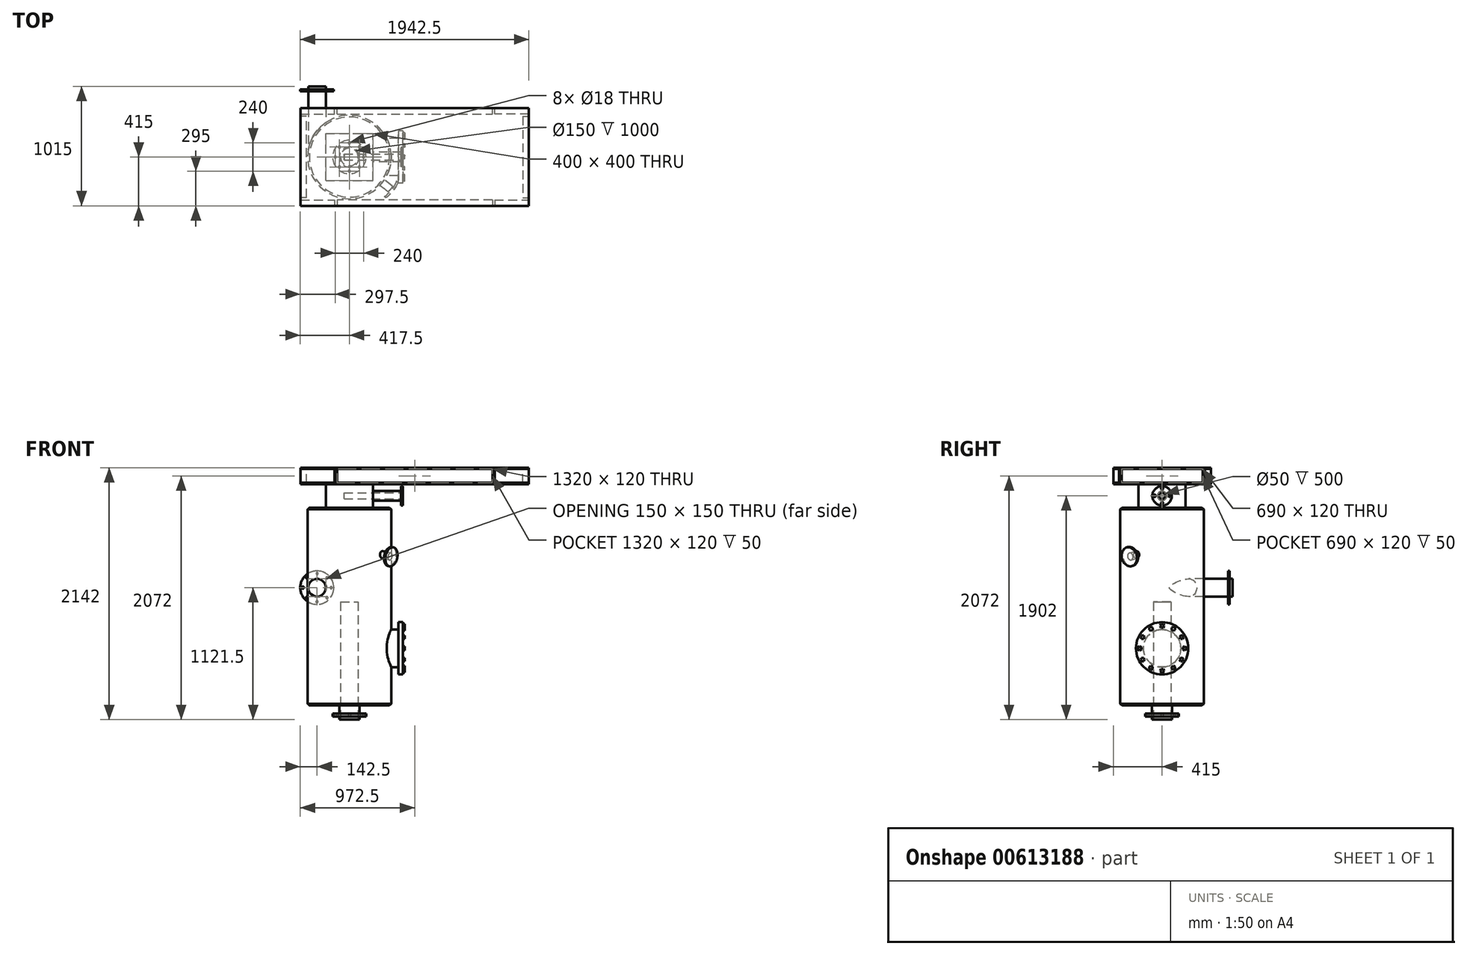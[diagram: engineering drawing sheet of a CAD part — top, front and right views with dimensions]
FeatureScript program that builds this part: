
annotation { "Feature Type Name" : "Feature", "Feature Type Description" : "" }
export const myFeature = defineFeature(function(context is Context, id is Id, definition is map)
    precondition{}
    {
        {
            var Q0;
            Q0=qCreatedBy(makeId("Front.planeOp"),FACE);
            var sketch = newSketch(context, id + "F0", { "sketchPlane" : qUnion([Q0])});
            skLineSegment(sketch, "E0.bottom", {"start": v(0, 0) * mm, "end": v(355, 0) * mm});
            skLineSegment(sketch, "E0.top", {"start": v(0, 1682) * mm, "end": v(355, 1682) * mm});
            skLineSegment(sketch, "E0.left", {"start": v(0, 0) * mm, "end": v(0, 1682) * mm});
            skLineSegment(sketch, "E0.right", {"start": v(355, 0) * mm, "end": v(355, 1682) * mm});
            skSolve(sketch);
        }
        {
            var Q0;
            Q0=makeQuery(id+"F0.imprint","IMPRINT",FACE,{"disambiguationData":[TD([[makeQuery(id+"F0.imprint","IMPRINT",EDGE,{"derivedFrom":sQuery(id+"F0.wireOp",EDGE,"E0.bottom")}),1.0]])]});
            var Q1;
            Q1=sQuery(id+"F0.wireOp",EDGE,"E0.left");
            revolve(context, id + "F1", {"entities" : qUnion([Q0]), "axis" : qUnion([Q1]), "revolveType" : RevolveType.FULL});
        }
        {
            var Q0;
            Q0=makeQuery(id+"F1.opRevolve","SWEPT_EDGE",EDGE,{"disambiguationData":[OSD([sQuery(id+"F0.wireOp",EDGE,"E0.top"),sQuery(id+"F0.wireOp",EDGE,"E0.right")])]});
            chamfer(context, id + "F2", {"entities" : qUnion([Q0]), "width" : 15 * mm, "tangentPropagation" : true});
        }
        {
            var Q0;
            Q0=qCreatedBy(makeId("Front.planeOp"),FACE);
            var sketch = newSketch(context, id + "F3", { "sketchPlane" : qUnion([Q0])});
            skCircle(sketch, "E1", {"center": v(-275, 1001.5) * mm, "radius": 75 * mm});
            skLineSegment(sketch, "E2", {"start": v(-355, 0) * mm, "end": v(-355, 1747) * mm});
            skSolve(sketch);
        }
        {
            var Q0;
            Q0 = qSketchRegion(id + "F3", true);
            extrude(context, id + "F4", {"entities" : qUnion([Q0]), "operationType" : NewBodyOperationType.ADD, "oppositeDirection" : true, "depth" : 600 * mm, "offsetDistance" : 25 * mm});
        }
        {
            var Q0;
            Q0=makeQuery(id+"F4.opExtrude","CAP_FACE",FACE,{"disambiguationData":[OSD([sQuery(id+"F3.wireOp",EDGE,"E1")])],"isStart":false});
            cPlane(context, id + "F5", {"entities" : qUnion([Q0]), "cplaneType" : CPlaneType.OFFSET, "offset" : 40 * mm, "oppositeDirection" : true, "width" : 150 * mm, "height" : 150 * mm});
        }
        {
            var Q0;
            Q0=qCreatedBy(id+"F5.planeOp",FACE);
            var sketch = newSketch(context, id + "F6", { "sketchPlane" : qUnion([Q0])});
            skCircle(sketch, "E3", {"center": v(275, 1001.5) * mm, "radius": 142.5 * mm});
            skSolve(sketch);
        }
        {
            var Q0;
            Q0=makeQuery(id+"F6.imprint","IMPRINT",FACE,{"disambiguationData":[TD([[makeQuery(id+"F6.imprint","IMPRINT",EDGE,{"derivedFrom":sQuery(id+"F6.wireOp",EDGE,"E3")}),1.0]])]});
            extrude(context, id + "F7", {"entities" : qUnion([Q0]), "operationType" : NewBodyOperationType.ADD, "depth" : 15 * mm, "offsetDistance" : 25 * mm});
        }
        {
            var Q0;
            Q0=makeQuery(id+"F7.opExtrude","CAP_FACE",FACE,{"disambiguationData":[OSD([sQuery(id+"F6.wireOp",EDGE,"E3")])],"isStart":false});
            var sketch = newSketch(context, id + "F8", { "sketchPlane" : qUnion([Q0])});
            skCircle(sketch, "E4", {"center": v(275.5, 881.5) * mm, "radius": 9 * mm});
            skCircle(sketch, "E5.1.0", {"center": v(360.21, 917) * mm, "radius": 9 * mm});
            skCircle(sketch, "E5.2.0", {"center": v(395, 1002) * mm, "radius": 9 * mm});
            skCircle(sketch, "E5.3.0", {"center": v(359.5, 1086.71) * mm, "radius": 9 * mm});
            skCircle(sketch, "E5.4.0", {"center": v(274.5, 1121.5) * mm, "radius": 9 * mm});
            skCircle(sketch, "E5.5.0", {"center": v(189.79, 1086) * mm, "radius": 9 * mm});
            skCircle(sketch, "E5.6.0", {"center": v(155, 1001) * mm, "radius": 9 * mm});
            skCircle(sketch, "E5.7.0", {"center": v(190.5, 916.29) * mm, "radius": 9 * mm});
            skPoint(sketch, "E5.center", {"position": v(275, 1001.5) * mm});
            skSolve(sketch);
        }
        {
            var Q0;
            Q0 = qSketchRegion(id + "F8", true);
            extrude(context, id + "F9", {"entities" : qUnion([Q0]), "operationType" : NewBodyOperationType.REMOVE, "oppositeDirection" : true, "depth" : 25 * mm, "offsetDistance" : 25 * mm});
        }
        {
            var Q0;
            Q0=qCreatedBy(makeId("Right.planeOp"),FACE);
            var sketch = newSketch(context, id + "F10", { "sketchPlane" : qUnion([Q0])});
            skCircle(sketch, "E6", {"center": v(0, 486) * mm, "radius": 160 * mm});
            skSolve(sketch);
        }
        {
            var Q0;
            Q0 = qSketchRegion(id + "F10", true);
            extrude(context, id + "F11", {"entities" : qUnion([Q0]), "operationType" : NewBodyOperationType.ADD, "depth" : 415 * mm, "offsetDistance" : 25 * mm});
        }
        {
            var Q0;
            Q0=makeQuery(id+"F11.opExtrude","CAP_FACE",FACE,{"disambiguationData":[OSD([sQuery(id+"F10.wireOp",EDGE,"E6")])],"isStart":false});
            var sketch = newSketch(context, id + "F12", { "sketchPlane" : qUnion([Q0])});
            skCircle(sketch, "E7", {"center": v(0, 486) * mm, "radius": 222.5 * mm});
            skSolve(sketch);
        }
        {
            var Q0;
            Q0=makeQuery(id+"F12.imprint","IMPRINT",FACE,{"disambiguationData":[TD([[makeQuery(id+"F12.imprint","IMPRINT",EDGE,{"derivedFrom":sQuery(id+"F12.wireOp",EDGE,"E7")}),1.0]])]});
            var Q1;
            Q1=makeQuery(id+"F12.imprint","IMPRINT",FACE,{"disambiguationData":[TD([[makeQuery(id+"F12.imprint","IMPRINT",EDGE,{"derivedFrom":makeQuery(id+"F11.opExtrude","CAP_EDGE",EDGE,{"disambiguationData":[OSD([sQuery(id+"F10.wireOp",EDGE,"E6")])],"isStart":false})}),1.0]])]});
            extrude(context, id + "F13", {"entities" : qUnion([Q0, Q1]), "operationType" : NewBodyOperationType.ADD, "depth" : 40 * mm, "offsetDistance" : 25 * mm});
        }
        {
            var Q0;
            Q0=makeQuery(id+"F13.opExtrude","CAP_FACE",FACE,{"disambiguationData":[OSD([sQuery(id+"F12.wireOp",EDGE,"E7")])],"isStart":false});
            var sketch = newSketch(context, id + "F14", { "sketchPlane" : qUnion([Q0])});
            skCircle(sketch, "E8.cCircle", {"center": v(0, 294.73) * mm, "radius": 14.58 * mm, "construction": true});
            skLineSegment(sketch, "E8.0", {"start": v(-8.42, 309.31) * mm, "end": v(8.42, 309.31) * mm});
            skLineSegment(sketch, "E8.1", {"start": v(8.42, 309.31) * mm, "end": v(16.84, 294.73) * mm});
            skLineSegment(sketch, "E8.2", {"start": v(16.84, 294.73) * mm, "end": v(8.42, 280.15) * mm});
            skLineSegment(sketch, "E8.3", {"start": v(8.42, 280.15) * mm, "end": v(-8.42, 280.15) * mm});
            skLineSegment(sketch, "E8.4", {"start": v(-8.42, 280.15) * mm, "end": v(-16.84, 294.73) * mm});
            skLineSegment(sketch, "E8.5", {"start": v(-16.84, 294.73) * mm, "end": v(-8.42, 309.31) * mm});
            skPoint(sketch, "E8.0.midPoint", {"position": v(0, 309.31) * mm});
            skCircle(sketch, "E9.1.0", {"center": v(95.63, 320.36) * mm, "radius": 14.58 * mm, "construction": true});
            skLineSegment(sketch, "E9.1.1", {"start": v(81.05, 311.94) * mm, "end": v(81.05, 328.78) * mm});
            skLineSegment(sketch, "E9.1.2", {"start": v(81.05, 328.78) * mm, "end": v(95.63, 337.2) * mm});
            skLineSegment(sketch, "E9.1.3", {"start": v(95.63, 337.2) * mm, "end": v(110.22, 328.78) * mm});
            skLineSegment(sketch, "E9.1.4", {"start": v(110.22, 328.78) * mm, "end": v(110.22, 311.94) * mm});
            skLineSegment(sketch, "E9.1.5", {"start": v(110.22, 311.94) * mm, "end": v(95.63, 303.52) * mm});
            skLineSegment(sketch, "E9.1.6", {"start": v(95.63, 303.52) * mm, "end": v(81.05, 311.94) * mm});
            skCircle(sketch, "E9.2.0", {"center": v(165.64, 390.37) * mm, "radius": 14.58 * mm, "construction": true});
            skLineSegment(sketch, "E9.2.1", {"start": v(157.22, 375.78) * mm, "end": v(148.8, 390.37) * mm});
            skLineSegment(sketch, "E9.2.2", {"start": v(148.8, 390.37) * mm, "end": v(157.22, 404.95) * mm});
            skLineSegment(sketch, "E9.2.3", {"start": v(157.22, 404.95) * mm, "end": v(174.06, 404.95) * mm});
            skLineSegment(sketch, "E9.2.4", {"start": v(174.06, 404.95) * mm, "end": v(182.48, 390.37) * mm});
            skLineSegment(sketch, "E9.2.5", {"start": v(182.48, 390.37) * mm, "end": v(174.06, 375.78) * mm});
            skLineSegment(sketch, "E9.2.6", {"start": v(174.06, 375.78) * mm, "end": v(157.22, 375.78) * mm});
            skCircle(sketch, "E9.3.0", {"center": v(191.27, 486) * mm, "radius": 14.58 * mm, "construction": true});
            skLineSegment(sketch, "E9.3.1", {"start": v(191.27, 469.16) * mm, "end": v(176.69, 477.58) * mm});
            skLineSegment(sketch, "E9.3.2", {"start": v(176.69, 477.58) * mm, "end": v(176.69, 494.42) * mm});
            skLineSegment(sketch, "E9.3.3", {"start": v(176.69, 494.42) * mm, "end": v(191.27, 502.84) * mm});
            skLineSegment(sketch, "E9.3.4", {"start": v(191.27, 502.84) * mm, "end": v(205.85, 494.42) * mm});
            skLineSegment(sketch, "E9.3.5", {"start": v(205.85, 494.42) * mm, "end": v(205.85, 477.58) * mm});
            skLineSegment(sketch, "E9.3.6", {"start": v(205.85, 477.58) * mm, "end": v(191.27, 469.16) * mm});
            skCircle(sketch, "E9.4.0", {"center": v(165.64, 581.63) * mm, "radius": 14.58 * mm, "construction": true});
            skLineSegment(sketch, "E9.4.1", {"start": v(174.06, 567.05) * mm, "end": v(157.22, 567.05) * mm});
            skLineSegment(sketch, "E9.4.2", {"start": v(157.22, 567.05) * mm, "end": v(148.8, 581.63) * mm});
            skLineSegment(sketch, "E9.4.3", {"start": v(148.8, 581.63) * mm, "end": v(157.22, 596.22) * mm});
            skLineSegment(sketch, "E9.4.4", {"start": v(157.22, 596.22) * mm, "end": v(174.06, 596.22) * mm});
            skLineSegment(sketch, "E9.4.5", {"start": v(174.06, 596.22) * mm, "end": v(182.48, 581.63) * mm});
            skLineSegment(sketch, "E9.4.6", {"start": v(182.48, 581.63) * mm, "end": v(174.06, 567.05) * mm});
            skCircle(sketch, "E9.5.0", {"center": v(95.63, 651.64) * mm, "radius": 14.58 * mm, "construction": true});
            skLineSegment(sketch, "E9.5.1", {"start": v(110.22, 643.22) * mm, "end": v(95.63, 634.8) * mm});
            skLineSegment(sketch, "E9.5.2", {"start": v(95.63, 634.8) * mm, "end": v(81.05, 643.22) * mm});
            skLineSegment(sketch, "E9.5.3", {"start": v(81.05, 643.22) * mm, "end": v(81.05, 660.06) * mm});
            skLineSegment(sketch, "E9.5.4", {"start": v(81.05, 660.06) * mm, "end": v(95.63, 668.48) * mm});
            skLineSegment(sketch, "E9.5.5", {"start": v(95.63, 668.48) * mm, "end": v(110.22, 660.06) * mm});
            skLineSegment(sketch, "E9.5.6", {"start": v(110.22, 660.06) * mm, "end": v(110.22, 643.22) * mm});
            skCircle(sketch, "E9.6.0", {"center": v(0, 677.27) * mm, "radius": 14.58 * mm, "construction": true});
            skLineSegment(sketch, "E9.6.1", {"start": v(16.84, 677.27) * mm, "end": v(8.42, 662.69) * mm});
            skLineSegment(sketch, "E9.6.2", {"start": v(8.42, 662.69) * mm, "end": v(-8.42, 662.69) * mm});
            skLineSegment(sketch, "E9.6.3", {"start": v(-8.42, 662.69) * mm, "end": v(-16.84, 677.27) * mm});
            skLineSegment(sketch, "E9.6.4", {"start": v(-16.84, 677.27) * mm, "end": v(-8.42, 691.85) * mm});
            skLineSegment(sketch, "E9.6.5", {"start": v(-8.42, 691.85) * mm, "end": v(8.42, 691.85) * mm});
            skLineSegment(sketch, "E9.6.6", {"start": v(8.42, 691.85) * mm, "end": v(16.84, 677.27) * mm});
            skCircle(sketch, "E9.7.0", {"center": v(-95.63, 651.64) * mm, "radius": 14.58 * mm, "construction": true});
            skLineSegment(sketch, "E9.7.1", {"start": v(-81.05, 660.06) * mm, "end": v(-81.05, 643.22) * mm});
            skLineSegment(sketch, "E9.7.2", {"start": v(-81.05, 643.22) * mm, "end": v(-95.63, 634.8) * mm});
            skLineSegment(sketch, "E9.7.3", {"start": v(-95.63, 634.8) * mm, "end": v(-110.22, 643.22) * mm});
            skLineSegment(sketch, "E9.7.4", {"start": v(-110.22, 643.22) * mm, "end": v(-110.22, 660.06) * mm});
            skLineSegment(sketch, "E9.7.5", {"start": v(-110.22, 660.06) * mm, "end": v(-95.63, 668.48) * mm});
            skLineSegment(sketch, "E9.7.6", {"start": v(-95.63, 668.48) * mm, "end": v(-81.05, 660.06) * mm});
            skCircle(sketch, "E9.8.0", {"center": v(-165.64, 581.63) * mm, "radius": 14.58 * mm, "construction": true});
            skLineSegment(sketch, "E9.8.1", {"start": v(-157.22, 596.22) * mm, "end": v(-148.8, 581.63) * mm});
            skLineSegment(sketch, "E9.8.2", {"start": v(-148.8, 581.63) * mm, "end": v(-157.22, 567.05) * mm});
            skLineSegment(sketch, "E9.8.3", {"start": v(-157.22, 567.05) * mm, "end": v(-174.06, 567.05) * mm});
            skLineSegment(sketch, "E9.8.4", {"start": v(-174.06, 567.05) * mm, "end": v(-182.48, 581.63) * mm});
            skLineSegment(sketch, "E9.8.5", {"start": v(-182.48, 581.63) * mm, "end": v(-174.06, 596.22) * mm});
            skLineSegment(sketch, "E9.8.6", {"start": v(-174.06, 596.22) * mm, "end": v(-157.22, 596.22) * mm});
            skCircle(sketch, "E9.9.0", {"center": v(-191.27, 486) * mm, "radius": 14.58 * mm, "construction": true});
            skLineSegment(sketch, "E9.9.1", {"start": v(-191.27, 502.84) * mm, "end": v(-176.69, 494.42) * mm});
            skLineSegment(sketch, "E9.9.2", {"start": v(-176.69, 494.42) * mm, "end": v(-176.69, 477.58) * mm});
            skLineSegment(sketch, "E9.9.3", {"start": v(-176.69, 477.58) * mm, "end": v(-191.27, 469.16) * mm});
            skLineSegment(sketch, "E9.9.4", {"start": v(-191.27, 469.16) * mm, "end": v(-205.85, 477.58) * mm});
            skLineSegment(sketch, "E9.9.5", {"start": v(-205.85, 477.58) * mm, "end": v(-205.85, 494.42) * mm});
            skLineSegment(sketch, "E9.9.6", {"start": v(-205.85, 494.42) * mm, "end": v(-191.27, 502.84) * mm});
            skCircle(sketch, "E9.10.0", {"center": v(-165.64, 390.37) * mm, "radius": 14.58 * mm, "construction": true});
            skLineSegment(sketch, "E9.10.1", {"start": v(-174.06, 404.95) * mm, "end": v(-157.22, 404.95) * mm});
            skLineSegment(sketch, "E9.10.2", {"start": v(-157.22, 404.95) * mm, "end": v(-148.8, 390.37) * mm});
            skLineSegment(sketch, "E9.10.3", {"start": v(-148.8, 390.37) * mm, "end": v(-157.22, 375.78) * mm});
            skLineSegment(sketch, "E9.10.4", {"start": v(-157.22, 375.78) * mm, "end": v(-174.06, 375.78) * mm});
            skLineSegment(sketch, "E9.10.5", {"start": v(-174.06, 375.78) * mm, "end": v(-182.48, 390.37) * mm});
            skLineSegment(sketch, "E9.10.6", {"start": v(-182.48, 390.37) * mm, "end": v(-174.06, 404.95) * mm});
            skCircle(sketch, "E9.11.0", {"center": v(-95.63, 320.36) * mm, "radius": 14.58 * mm, "construction": true});
            skLineSegment(sketch, "E9.11.1", {"start": v(-110.22, 328.78) * mm, "end": v(-95.63, 337.2) * mm});
            skLineSegment(sketch, "E9.11.2", {"start": v(-95.63, 337.2) * mm, "end": v(-81.05, 328.78) * mm});
            skLineSegment(sketch, "E9.11.3", {"start": v(-81.05, 328.78) * mm, "end": v(-81.05, 311.94) * mm});
            skLineSegment(sketch, "E9.11.4", {"start": v(-81.05, 311.94) * mm, "end": v(-95.63, 303.52) * mm});
            skLineSegment(sketch, "E9.11.5", {"start": v(-95.63, 303.52) * mm, "end": v(-110.22, 311.94) * mm});
            skLineSegment(sketch, "E9.11.6", {"start": v(-110.22, 311.94) * mm, "end": v(-110.22, 328.78) * mm});
            skPoint(sketch, "E9.center", {"position": v(0, 486) * mm});
            skSolve(sketch);
        }
        {
            var Q0;
            Q0 = qSketchRegion(id + "F14", true);
            extrude(context, id + "F15", {"entities" : qUnion([Q0]), "operationType" : NewBodyOperationType.ADD, "depth" : 15 * mm, "offsetDistance" : 25 * mm});
        }
        {
            var Q0;
            Q0=makeQuery(id+"F1.opRevolve","SWEPT_EDGE",EDGE,{"disambiguationData":[OSD([sQuery(id+"F0.wireOp",EDGE,"E0.bottom"),sQuery(id+"F0.wireOp",EDGE,"E0.right")])]});
            chamfer(context, id + "F16", {"entities" : qUnion([Q0]), "width" : 15 * mm, "tangentPropagation" : true});
        }
        {
            var Q0;
            Q0=makeQuery(id+"F1.opRevolve","SWEPT_FACE",FACE,{"disambiguationData":[OSD([sQuery(id+"F0.wireOp",EDGE,"E0.bottom")])]});
            var sketch = newSketch(context, id + "F17", { "sketchPlane" : qUnion([Q0])});
            skCircle(sketch, "E10", {"center": v(0, 0) * mm, "radius": 85 * mm});
            skSolve(sketch);
        }
        {
            var Q0;
            Q0 = qSketchRegion(id + "F17", true);
            extrude(context, id + "F18", {"entities" : qUnion([Q0]), "operationType" : NewBodyOperationType.ADD, "depth" : 120 * mm, "offsetDistance" : 25 * mm});
        }
        {
            var Q0;
            Q0=makeQuery(id+"F18.opExtrude","CAP_FACE",FACE,{"disambiguationData":[OSD([sQuery(id+"F17.wireOp",EDGE,"E10")])],"isStart":false});
            cPlane(context, id + "F19", {"entities" : qUnion([Q0]), "cplaneType" : CPlaneType.OFFSET, "offset" : 25 * mm, "oppositeDirection" : true, "width" : 150 * mm, "height" : 150 * mm});
        }
        {
            var Q0;
            Q0=qCreatedBy(id+"F19.planeOp",FACE);
            var sketch = newSketch(context, id + "F20", { "sketchPlane" : qUnion([Q0])});
            skCircle(sketch, "E11", {"center": v(0, 0) * mm, "radius": 142.5 * mm});
            skSolve(sketch);
        }
        {
            var Q0;
            Q0 = qSketchRegion(id + "F20", true);
            extrude(context, id + "F21", {"entities" : qUnion([Q0]), "operationType" : NewBodyOperationType.ADD, "oppositeDirection" : true, "depth" : 25 * mm, "offsetDistance" : 25 * mm});
        }
        {
            var Q0;
            Q0=makeQuery(id+"F21.opExtrude","CAP_FACE",FACE,{"disambiguationData":[OSD([sQuery(id+"F20.wireOp",EDGE,"E11")])],"isStart":true});
            var sketch = newSketch(context, id + "F22", { "sketchPlane" : qUnion([Q0])});
            skCircle(sketch, "E12", {"center": v(0, 120) * mm, "radius": 9 * mm});
            skCircle(sketch, "E13.1.0", {"center": v(-84.85, 84.85) * mm, "radius": 9 * mm});
            skCircle(sketch, "E13.2.0", {"center": v(-120, 0) * mm, "radius": 9 * mm});
            skCircle(sketch, "E13.3.0", {"center": v(-84.85, -84.85) * mm, "radius": 9 * mm});
            skCircle(sketch, "E13.4.0", {"center": v(0, -120) * mm, "radius": 9 * mm});
            skCircle(sketch, "E13.5.0", {"center": v(84.85, -84.85) * mm, "radius": 9 * mm});
            skCircle(sketch, "E13.6.0", {"center": v(120, 0) * mm, "radius": 9 * mm});
            skCircle(sketch, "E13.7.0", {"center": v(84.85, 84.85) * mm, "radius": 9 * mm});
            skPoint(sketch, "E13.center", {"position": v(0, 0) * mm});
            skSolve(sketch);
        }
        {
            var Q0;
            Q0 = qSketchRegion(id + "F22", true);
            extrude(context, id + "F23", {"entities" : qUnion([Q0]), "operationType" : NewBodyOperationType.REMOVE, "oppositeDirection" : true, "depth" : 25 * mm, "offsetDistance" : 25 * mm});
        }
        {
            var Q0;
            Q0=makeQuery(id+"F1.opRevolve","SWEPT_FACE",FACE,{"disambiguationData":[OSD([sQuery(id+"F0.wireOp",EDGE,"E0.top")])]});
            var sketch = newSketch(context, id + "F24", { "sketchPlane" : qUnion([Q0])});
            skLineSegment(sketch, "E14.bottom", {"start": v(-200, -200) * mm, "end": v(200, -200) * mm});
            skLineSegment(sketch, "E14.top", {"start": v(-200, 200) * mm, "end": v(200, 200) * mm});
            skLineSegment(sketch, "E14.left", {"start": v(-200, -200) * mm, "end": v(-200, 200) * mm});
            skLineSegment(sketch, "E14.right", {"start": v(200, -200) * mm, "end": v(200, 200) * mm});
            skPoint(sketch, "E14.middle", {"position": v(0, 0) * mm});
            skSolve(sketch);
        }
        {
            var Q0;
            Q0 = qSketchRegion(id + "F24", true);
            extrude(context, id + "F25", {"entities" : qUnion([Q0]), "operationType" : NewBodyOperationType.ADD, "depth" : 200 * mm, "offsetDistance" : 25 * mm});
        }
        {
            var Q0;
            Q0=makeQuery(id+"F25.opExtrude","CAP_FACE",FACE,{"disambiguationData":[OSD([sQuery(id+"F24.wireOp",EDGE,"E14.bottom"),sQuery(id+"F24.wireOp",EDGE,"E14.top"),sQuery(id+"F24.wireOp",EDGE,"E14.left"),sQuery(id+"F24.wireOp",EDGE,"E14.right")])],"isStart":false});
            var sketch = newSketch(context, id + "F26", { "sketchPlane" : qUnion([Q0])});
            skLineSegment(sketch, "E15.bottom", {"start": v(-415, 415) * mm, "end": v(1525, 415) * mm});
            skLineSegment(sketch, "E15.top", {"start": v(-415, -415) * mm, "end": v(1525, -415) * mm});
            skLineSegment(sketch, "E15.left", {"start": v(-415, 415) * mm, "end": v(-415, -415) * mm});
            skLineSegment(sketch, "E15.right", {"start": v(1525, 415) * mm, "end": v(1525, -415) * mm});
            skSolve(sketch);
        }
        {
            var Q0;
            Q0 = qSketchRegion(id + "F26", true);
            extrude(context, id + "F27", {"entities" : qUnion([Q0]), "operationType" : NewBodyOperationType.ADD, "depth" : 140 * mm, "offsetDistance" : 25 * mm});
        }
        {
            var Q0;
            Q0=qCreatedBy(makeId("Front.planeOp"),FACE);
            var sketch = newSketch(context, id + "F28", { "sketchPlane" : qUnion([Q0])});
            skLineSegment(sketch, "E16", {"start": v(0, 0) * mm, "end": v(0, -161.72) * mm});
            skSolve(sketch);
        }
        {
            var Q0;
            Q0=sQuery(id+"F28.wireOp",EDGE,"E16");
            cPlane(context, id + "F29", {"entities" : qUnion([Q0]), "cplaneType" : CPlaneType.LINE_ANGLE, "offset" : 25 * mm, "angle" : 38 * degree, "width" : 150 * mm, "height" : 150 * mm});
        }
        {
            var Q0;
            Q0=qCreatedBy(id+"F29.planeOp",FACE);
            cPlane(context, id + "F30", {"entities" : qUnion([Q0]), "cplaneType" : CPlaneType.OFFSET, "offset" : 340 * mm, "oppositeDirection" : true, "width" : 150 * mm, "height" : 150 * mm});
        }
        {
            var Q0;
            Q0=qCreatedBy(id+"F30.planeOp",FACE);
            var sketch = newSketch(context, id + "F31", { "sketchPlane" : qUnion([Q0])});
            skLineSegment(sketch, "E17", {"start": v(0, 1281.3) * mm, "end": v(148.15, 1281.3) * mm});
            skSolve(sketch);
        }
        {
            var Q0;
            Q0=sQuery(id+"F31.wireOp",EDGE,"E17");
            cPlane(context, id + "F32", {"entities" : qUnion([Q0]), "cplaneType" : CPlaneType.LINE_ANGLE, "offset" : 25 * mm, "angle" : 80 * degree, "width" : 150 * mm, "height" : 150 * mm});
        }
        {
            var Q0;
            Q0=qCreatedBy(id+"F32.planeOp",FACE);
            var sketch = newSketch(context, id + "F33", { "sketchPlane" : qUnion([Q0])});
            skCircle(sketch, "E18", {"center": v(-177.95, 1311.44) * mm, "radius": 30 * mm});
            skSolve(sketch);
        }
        {
            var Q0;
            Q0 = qSketchRegion(id + "F33", true);
            extrude(context, id + "F34", {"entities" : qUnion([Q0]), "operationType" : NewBodyOperationType.ADD, "depth" : 100 * mm, "offsetDistance" : 25 * mm});
        }
        {
            var Q0;
            Q0=makeQuery(id+"F34.opExtrude","CAP_FACE",FACE,{"disambiguationData":[OSD([sQuery(id+"F33.wireOp",EDGE,"E18")])],"isStart":false});
            var sketch = newSketch(context, id + "F35", { "sketchPlane" : qUnion([Q0])});
            skCircle(sketch, "E19", {"center": v(-177.95, 1311.44) * mm, "radius": 82.5 * mm});
            skSolve(sketch);
        }
        {
            var Q0;
            Q0 = qSketchRegion(id + "F35", true);
            extrude(context, id + "F36", {"entities" : qUnion([Q0]), "operationType" : NewBodyOperationType.ADD, "depth" : 15 * mm, "offsetDistance" : 25 * mm});
        }
        {
            var Q0;
            Q0=makeQuery(id+"F27.opExtrude","SWEPT_FACE",FACE,{"disambiguationData":[OSD([sQuery(id+"F26.wireOp",EDGE,"E15.bottom")])]});
            var sketch = newSketch(context, id + "F37", { "sketchPlane" : qUnion([Q0])});
            skLineSegment(sketch, "E20.bottom", {"start": v(105, 1892) * mm, "end": v(-1215, 1892) * mm});
            skLineSegment(sketch, "E20.top", {"start": v(105, 2012) * mm, "end": v(-1215, 2012) * mm});
            skLineSegment(sketch, "E20.left", {"start": v(105, 1892) * mm, "end": v(105, 2012) * mm});
            skLineSegment(sketch, "E20.right", {"start": v(-1215, 1892) * mm, "end": v(-1215, 2012) * mm});
            skLineSegment(sketch, "E21.bottom", {"start": v(415, 1892) * mm, "end": v(125, 1892) * mm});
            skLineSegment(sketch, "E21.top", {"start": v(415, 2012) * mm, "end": v(125, 2012) * mm});
            skLineSegment(sketch, "E21.left", {"start": v(415, 1892) * mm, "end": v(415, 2012) * mm});
            skLineSegment(sketch, "E21.right", {"start": v(125, 1892) * mm, "end": v(125, 2012) * mm});
            skLineSegment(sketch, "E22.bottom", {"start": v(-1525, 1892) * mm, "end": v(-1235, 1892) * mm});
            skLineSegment(sketch, "E22.top", {"start": v(-1525, 2012) * mm, "end": v(-1235, 2012) * mm});
            skLineSegment(sketch, "E22.left", {"start": v(-1525, 1892) * mm, "end": v(-1525, 2012) * mm});
            skLineSegment(sketch, "E22.right", {"start": v(-1235, 1892) * mm, "end": v(-1235, 2012) * mm});
            skSolve(sketch);
        }
        {
            var Q0;
            Q0 = qSketchRegion(id + "F37", true);
            extrude(context, id + "F38", {"entities" : qUnion([Q0]), "operationType" : NewBodyOperationType.REMOVE, "oppositeDirection" : true, "depth" : 50 * mm, "offsetDistance" : 25 * mm});
        }
        {
            var Q0;
            Q0=makeQuery(id+"F27.opExtrude","SWEPT_FACE",FACE,{"disambiguationData":[OSD([sQuery(id+"F26.wireOp",EDGE,"E15.top")])]});
            var sketch = newSketch(context, id + "F39", { "sketchPlane" : qUnion([Q0])});
            skLineSegment(sketch, "E23.0.0", {"start": v(1235, 2012) * mm, "end": v(1525, 2012) * mm});
            skLineSegment(sketch, "E23.0.1", {"start": v(1525, 2012) * mm, "end": v(1525, 1892) * mm});
            skLineSegment(sketch, "E23.0.2", {"start": v(1525, 1892) * mm, "end": v(1235, 1892) * mm});
            skLineSegment(sketch, "E23.0.3", {"start": v(1235, 1892) * mm, "end": v(1235, 2012) * mm});
            skLineSegment(sketch, "E24.0.0", {"start": v(-105, 1892) * mm, "end": v(-105, 2012) * mm});
            skLineSegment(sketch, "E24.0.1", {"start": v(-105, 2012) * mm, "end": v(1215, 2012) * mm});
            skLineSegment(sketch, "E24.0.2", {"start": v(1215, 2012) * mm, "end": v(1215, 1892) * mm});
            skLineSegment(sketch, "E24.0.3", {"start": v(1215, 1892) * mm, "end": v(-105, 1892) * mm});
            skLineSegment(sketch, "E25.0.0", {"start": v(-415, 1892) * mm, "end": v(-415, 2012) * mm});
            skLineSegment(sketch, "E25.0.1", {"start": v(-415, 2012) * mm, "end": v(-125, 2012) * mm});
            skLineSegment(sketch, "E25.0.2", {"start": v(-125, 2012) * mm, "end": v(-125, 1892) * mm});
            skLineSegment(sketch, "E25.0.3", {"start": v(-125, 1892) * mm, "end": v(-415, 1892) * mm});
            skSolve(sketch);
        }
        {
            var Q0;
            Q0 = qSketchRegion(id + "F39", true);
            extrude(context, id + "F40", {"entities" : qUnion([Q0]), "operationType" : NewBodyOperationType.REMOVE, "oppositeDirection" : true, "depth" : 50 * mm, "offsetDistance" : 25 * mm});
        }
        {
            var Q0;
            Q0=makeQuery(id+"F27.opExtrude","SWEPT_FACE",FACE,{"disambiguationData":[OSD([sQuery(id+"F26.wireOp",EDGE,"E15.right")])]});
            var sketch = newSketch(context, id + "F41", { "sketchPlane" : qUnion([Q0])});
            skLineSegment(sketch, "E26.bottom", {"start": v(345, 1892) * mm, "end": v(-345, 1892) * mm});
            skLineSegment(sketch, "E26.top", {"start": v(345, 2012) * mm, "end": v(-345, 2012) * mm});
            skLineSegment(sketch, "E26.left", {"start": v(345, 1892) * mm, "end": v(345, 2012) * mm});
            skLineSegment(sketch, "E26.right", {"start": v(-345, 1892) * mm, "end": v(-345, 2012) * mm});
            skSolve(sketch);
        }
        {
            var Q0;
            Q0=makeQuery(id+"F41.imprint","IMPRINT",FACE,{"disambiguationData":[TD([[makeQuery(id+"F41.imprint","IMPRINT",EDGE,{"derivedFrom":sQuery(id+"F41.wireOp",EDGE,"E26.bottom")}),-1.0]])]});
            extrude(context, id + "F42", {"entities" : qUnion([Q0]), "operationType" : NewBodyOperationType.REMOVE, "oppositeDirection" : true, "depth" : 50 * mm, "offsetDistance" : 25 * mm});
        }
        {
            var Q0;
            Q0=makeQuery(id+"F27.opExtrude","SWEPT_FACE",FACE,{"disambiguationData":[OSD([sQuery(id+"F26.wireOp",EDGE,"E15.left")])]});
            var sketch = newSketch(context, id + "F43", { "sketchPlane" : qUnion([Q0])});
            skLineSegment(sketch, "E27.0.0", {"start": v(-345, 1892) * mm, "end": v(-345, 2012) * mm});
            skLineSegment(sketch, "E27.0.1", {"start": v(-345, 2012) * mm, "end": v(345, 2012) * mm});
            skLineSegment(sketch, "E27.0.2", {"start": v(345, 2012) * mm, "end": v(345, 1892) * mm});
            skLineSegment(sketch, "E27.0.3", {"start": v(345, 1892) * mm, "end": v(-345, 1892) * mm});
            skSolve(sketch);
        }
        {
            var Q0;
            Q0=makeQuery(id+"F43.imprint","IMPRINT",FACE,{"disambiguationData":[TD([[makeQuery(id+"F43.imprint","IMPRINT",EDGE,{"derivedFrom":sQuery(id+"F43.wireOp",EDGE,"E27.0.0")}),-1.0]])]});
            extrude(context, id + "F44", {"entities" : qUnion([Q0]), "operationType" : NewBodyOperationType.REMOVE, "oppositeDirection" : true, "depth" : 50 * mm, "offsetDistance" : 25 * mm});
        }
        {
            var Q0;
            Q0=makeQuery(id+"F25.opExtrude","SWEPT_FACE",FACE,{"disambiguationData":[OSD([sQuery(id+"F24.wireOp",EDGE,"E14.right")])]});
            var sketch = newSketch(context, id + "F45", { "sketchPlane" : qUnion([Q0])});
            skCircle(sketch, "E28", {"center": v(0, 1782) * mm, "radius": 40 * mm});
            skSolve(sketch);
        }
        {
            var Q0;
            Q0=makeQuery(id+"F45.imprint","IMPRINT",FACE,{"disambiguationData":[TD([[makeQuery(id+"F45.imprint","IMPRINT",EDGE,{"derivedFrom":sQuery(id+"F45.wireOp",EDGE,"E28")}),1.0]])]});
            extrude(context, id + "F46", {"entities" : qUnion([Q0]), "operationType" : NewBodyOperationType.ADD, "depth" : 240 * mm, "offsetDistance" : 25 * mm});
        }
        {
            var Q0;
            Q0=makeQuery(id+"F46.opExtrude","CAP_FACE",FACE,{"disambiguationData":[OSD([sQuery(id+"F45.wireOp",EDGE,"E28")])],"isStart":false});
            var sketch = newSketch(context, id + "F47", { "sketchPlane" : qUnion([Q0])});
            skCircle(sketch, "E29", {"center": v(0, 1782) * mm, "radius": 82.5 * mm});
            skSolve(sketch);
        }
        {
            var Q0;
            Q0 = qSketchRegion(id + "F47", true);
            extrude(context, id + "F48", {"entities" : qUnion([Q0]), "operationType" : NewBodyOperationType.ADD, "depth" : 15 * mm, "offsetDistance" : 25 * mm});
        }
        {
            var Q0;
            Q0=makeQuery(id+"F48.opExtrude","CAP_FACE",FACE,{"disambiguationData":[OSD([sQuery(id+"F47.wireOp",EDGE,"E29")])],"isStart":false});
            var sketch = newSketch(context, id + "F49", { "sketchPlane" : qUnion([Q0])});
            skCircle(sketch, "E30", {"center": v(0, 1719.5) * mm, "radius": 9 * mm});
            skCircle(sketch, "E31.1.0", {"center": v(62.5, 1782) * mm, "radius": 9 * mm});
            skCircle(sketch, "E31.2.0", {"center": v(0, 1844.5) * mm, "radius": 9 * mm});
            skCircle(sketch, "E31.3.0", {"center": v(-62.5, 1782) * mm, "radius": 9 * mm});
            skPoint(sketch, "E31.center", {"position": v(0, 1782) * mm});
            skSolve(sketch);
        }
        {
            var Q0;
            Q0 = qSketchRegion(id + "F49", true);
            extrude(context, id + "F50", {"entities" : qUnion([Q0]), "operationType" : NewBodyOperationType.REMOVE, "oppositeDirection" : true, "depth" : 25 * mm, "offsetDistance" : 25 * mm});
        }
        {
            var Q0;
            Q0=makeQuery(id+"F48.opExtrude","CAP_FACE",FACE,{"disambiguationData":[OSD([sQuery(id+"F47.wireOp",EDGE,"E29")])],"isStart":false});
            var sketch = newSketch(context, id + "F51", { "sketchPlane" : qUnion([Q0])});
            skCircle(sketch, "E32", {"center": v(0, 1782) * mm, "radius": 25 * mm});
            skSolve(sketch);
        }
        {
            var Q0;
            Q0=makeQuery(id+"F51.imprint","IMPRINT",FACE,{"disambiguationData":[TD([[makeQuery(id+"F51.imprint","IMPRINT",EDGE,{"derivedFrom":sQuery(id+"F51.wireOp",EDGE,"E32")}),1.0]])]});
            extrude(context, id + "F52", {"entities" : qUnion([Q0]), "operationType" : NewBodyOperationType.REMOVE, "oppositeDirection" : true, "depth" : 500 * mm, "offsetDistance" : 25 * mm});
        }
        {
            var Q0;
            Q0=makeQuery(id+"F18.opExtrude","CAP_FACE",FACE,{"disambiguationData":[OSD([sQuery(id+"F17.wireOp",EDGE,"E10")])],"isStart":false});
            var sketch = newSketch(context, id + "F53", { "sketchPlane" : qUnion([Q0])});
            skCircle(sketch, "E33", {"center": v(0, 0) * mm, "radius": 75 * mm});
            skSolve(sketch);
        }
        {
            var Q0;
            Q0=makeQuery(id+"F53.imprint","IMPRINT",FACE,{"disambiguationData":[TD([[makeQuery(id+"F53.imprint","IMPRINT",EDGE,{"derivedFrom":sQuery(id+"F53.wireOp",EDGE,"E33")}),1.0]])]});
            extrude(context, id + "F54", {"entities" : qUnion([Q0]), "operationType" : NewBodyOperationType.REMOVE, "oppositeDirection" : true, "depth" : 1000 * mm, "offsetDistance" : 25 * mm});
        }
    });
